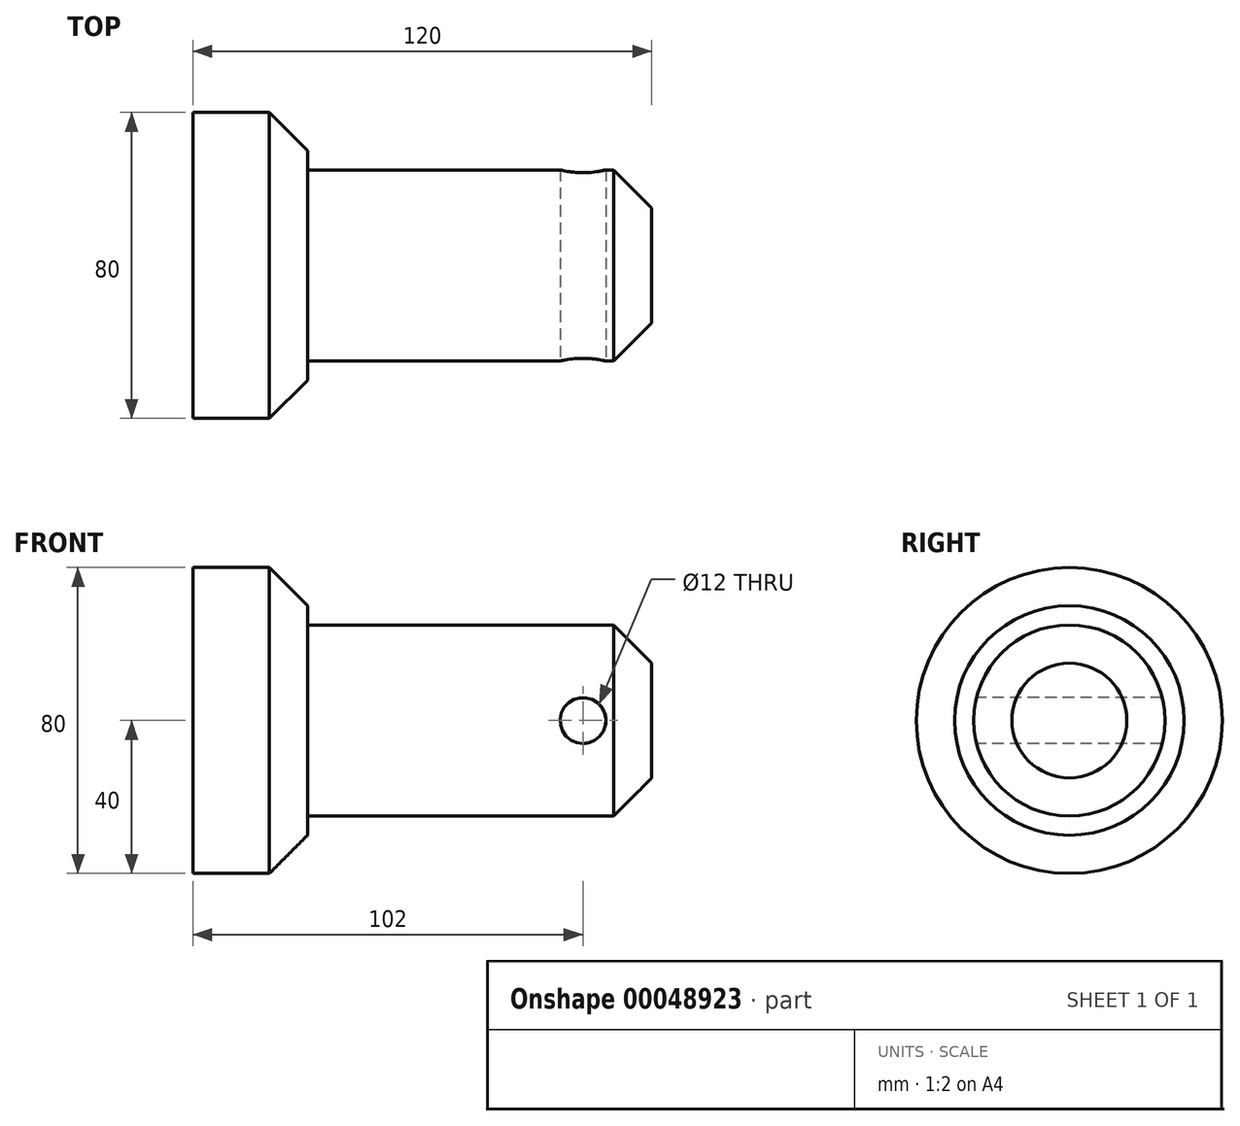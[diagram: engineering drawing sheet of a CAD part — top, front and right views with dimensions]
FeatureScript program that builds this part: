
annotation { "Feature Type Name" : "Feature", "Feature Type Description" : "" }
export const myFeature = defineFeature(function(context is Context, id is Id, definition is map)
    precondition{}
    {
        {
            var Q0;
            Q0=qCreatedBy(makeId("Front.planeOp"),FACE);
            var sketch = newSketch(context, id + "F0", { "sketchPlane" : qUnion([Q0])});
            skLineSegment(sketch, "E0", {"start": v(0, 0) * mm, "end": v(-120, 0) * mm, "construction": true});
            skLineSegment(sketch, "E1", {"start": v(-120, 0) * mm, "end": v(-120, 40) * mm});
            skLineSegment(sketch, "E2", {"start": v(0, 57.36) * mm, "end": v(-90, 57.36) * mm, "construction": true});
            skLineSegment(sketch, "E3", {"start": v(-90, 0) * mm, "end": v(-90, 25) * mm, "construction": true});
            skLineSegment(sketch, "E4", {"start": v(-120, 40) * mm, "end": v(-90, 40) * mm});
            skLineSegment(sketch, "E5", {"start": v(-90, 40) * mm, "end": v(-90, 25) * mm});
            skLineSegment(sketch, "E6", {"start": v(-90, 25) * mm, "end": v(0, 25) * mm});
            skLineSegment(sketch, "E7", {"start": v(0, 25) * mm, "end": v(0, 0) * mm});
            skLineSegment(sketch, "E8", {"start": v(-120, 0) * mm, "end": v(0, 0) * mm});
            skLineSegment(sketch, "E9", {"start": v(-90, 0) * mm, "end": v(-15, 0) * mm, "construction": true});
            skSolve(sketch);
        }
        {
            var Q0;
            Q0=makeQuery(id+"F0.imprint","IMPRINT",FACE,{"disambiguationData":[TD([[makeQuery(id+"F0.imprint","IMPRINT",EDGE,{"derivedFrom":sQuery(id+"F0.wireOp",EDGE,"E1")}),-1.0]])]});
            var Q1;
            Q1=sQuery(id+"F0.wireOp",EDGE,"E8");
            revolve(context, id + "F1", {"entities" : qUnion([Q0]), "axis" : qUnion([Q1]), "revolveType" : RevolveType.FULL});
        }
        {
            var Q0;
            Q0=makeQuery(id+"F1.opRevolve","SWEPT_EDGE",EDGE,{"disambiguationData":[OSD([sQuery(id+"F0.wireOp",EDGE,"E4"),sQuery(id+"F0.wireOp",EDGE,"E5")])]});
            chamfer(context, id + "F2", {"entities" : qUnion([Q0]), "width" : 10 * mm, "tangentPropagation" : true});
        }
        {
            var Q0;
            Q0=makeQuery(id+"F1.opRevolve","SWEPT_EDGE",EDGE,{"disambiguationData":[OSD([sQuery(id+"F0.wireOp",EDGE,"E6"),sQuery(id+"F0.wireOp",EDGE,"E7")])]});
            chamfer(context, id + "F3", {"entities" : qUnion([Q0]), "width" : 10 * mm, "tangentPropagation" : true});
        }
        {
            var Q0;
            Q0=qCreatedBy(makeId("Front.planeOp"),FACE);
            var sketch = newSketch(context, id + "F4", { "sketchPlane" : qUnion([Q0])});
            skCircle(sketch, "E10", {"center": v(-18, 0) * mm, "radius": 6 * mm});
            skSolve(sketch);
        }
        {
            var Q0;
            Q0 = qSketchRegion(id + "F4", true);
            extrude(context, id + "F5", {"entities" : qUnion([Q0]), "operationType" : NewBodyOperationType.REMOVE, "endBound" : BoundingType.THROUGH_ALL, "oppositeDirection" : true, "depth" : 25 * mm, "hasSecondDirection" : true, "secondDirectionBound" : SecondDirectionBoundingType.THROUGH_ALL, "secondDirectionOppositeDirection" : false, "secondDirectionDepth" : 25 * mm});
        }
    });
